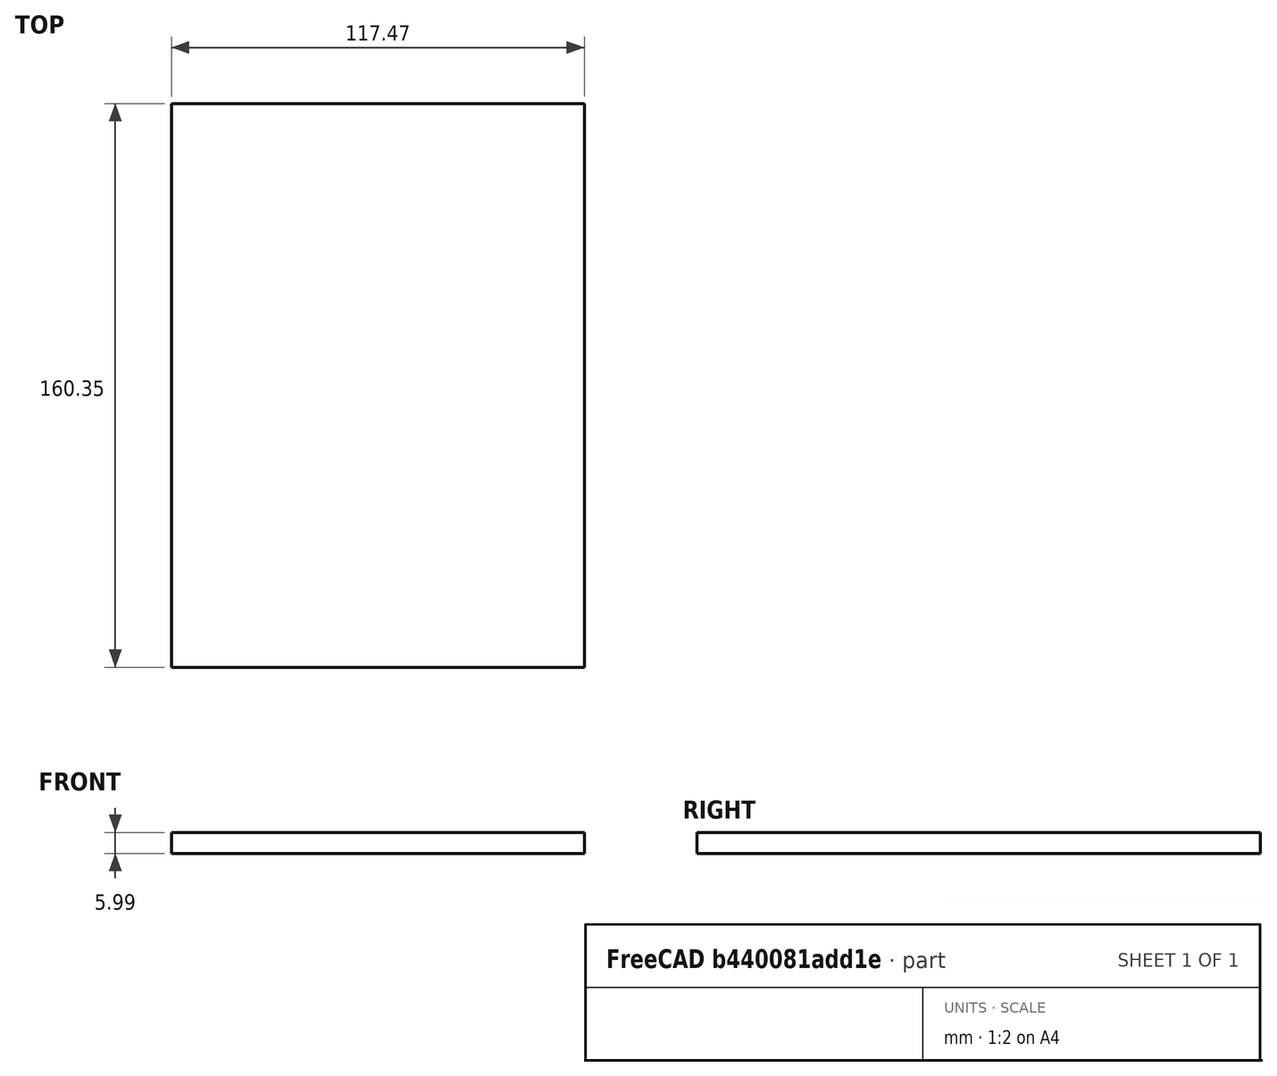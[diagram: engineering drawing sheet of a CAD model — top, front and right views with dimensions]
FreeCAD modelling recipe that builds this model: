
FCSTD DOCUMENT  (FreeCAD 0.19R24267 (Git))
Label: Inv2-P11
License: All rights reserved
LicenseURL: http://en.wikipedia.org/wiki/All_rights_reserved
objects: TechDraw::DrawViewDimension×3, TechDraw::DrawProjGroupItem×2, TechDraw::DrawHatch×2, TechDraw::DrawViewAnnotation×2, Sketcher::SketchObject×1, Part::Extrusion×1, TechDraw::DrawSVGTemplate×1, TechDraw::DrawProjGroup×1, TechDraw::DrawPage×1
note: 2 computed .brp shape members not serialized (recipe doc carries the construction recipe); baked Part::Feature solids carry a one-line shape summary decoded from their .brp

FEATURE [Sketcher::SketchObject] Sketch
  FullyConstrained = true
  sketch-geometry (4):
    g0: LineSegment StartX=0 StartY=0 StartZ=0 EndX=117.475 EndY=0 EndZ=0
    g1: LineSegment StartX=117.475 StartY=0 StartZ=0 EndX=117.475 EndY=-160.35 EndZ=0
    g2: LineSegment StartX=117.475 StartY=-160.35 StartZ=0 EndX=0 EndY=-160.35 EndZ=0
    g3: LineSegment StartX=0 StartY=-160.35 StartZ=0 EndX=0 EndY=0 EndZ=0
  constraints (11):
    c: Coincident(g0,g1)
    c: Coincident(g1,g2)
    c: Coincident(g2,g3)
    c: Coincident(g3,g0)
    c: Horizontal(g0)
    c: Horizontal(g2)
    c: Vertical(g1)
    c: Vertical(g3)
    c: DistanceX(g2,g2) = 117.475
    c: DistanceY(g3,g3) = 160.35
    c: Coincident(g-1,g0)
FEATURE [Part::Extrusion] Extrude
  Base = -> Sketch
  Dir = (0,0,1)
  DirMode = 2
  FaceMakerClass = Part::FaceMakerBullseye
  LengthFwd = 5.9944
  LengthRev = 0
  Solid = true
  Symmetric = false
FEATURE [TechDraw::DrawSVGTemplate] Template
  Height = 215.9
  Orientation = 1
  Width = 279.4
FEATURE [TechDraw::DrawProjGroupItem] ProjItem  label="Front"
  CoarseView = false
  Direction = (0,0,1)
  Focus = 100
  HardHidden = false
  IsoCount = 0
  IsoHidden = false
  IsoVisible = false
  LockPosition = true
  Perspective = false
  Rotation = 0
  RotationVector = (1,0,0)
  Scale = 0.5
  ScaleType = 2
  SeamHidden = false
  SeamVisible = true
  SmoothHidden = false
  SmoothVisible = true
  Source = -> [Extrude]
  Type = 0
  X = 0
  XDirection = (1,0,0)
  Y = 0
FEATURE [TechDraw::DrawProjGroupItem] ProjItem001  label="Left"
  CoarseView = false
  Direction = (-1,0,1e-16)
  Focus = 100
  HardHidden = false
  IsoCount = 0
  IsoHidden = false
  IsoVisible = false
  LockPosition = false
  Perspective = false
  Rotation = 0
  RotationVector = (1,0,0)
  ScaleType = 2
  SeamHidden = false
  SeamVisible = true
  SmoothHidden = false
  SmoothVisible = true
  Source = -> [Extrude]
  Type = 1
  X = 60.3352
  XDirection = (1e-16,0,1)
  Y = 0
FEATURE [TechDraw::DrawProjGroup] ProjGroup
  Anchor = -> ProjItem
  AutoDistribute = true
  LockPosition = false
  ProjectionType = 0
  Rotation = 0
  Scale = 0.5
  ScaleType = 2
  Source = -> [Extrude]
  Views = -> [ProjItem,ProjItem001]
  X = 131.036
  Y = 108.959
  spacingX = 15.0114
  spacingY = 15.0114
FEATURE [TechDraw::DrawHatch] Hatch  label="HatchF0"
  HatchPattern = <path>
  Source = -> ProjItem [Face0]
FEATURE [TechDraw::DrawHatch] Hatch001  label="Hatch001F0"
  HatchPattern = <path>
  Source = -> ProjItem001 [Face0]
FEATURE [TechDraw::DrawViewDimension] Dimension
  Arbitrary = false
  ArbitraryTolerances = false
  EqualTolerance = true
  FormatSpec = %.3f
  FormatSpecOverTolerance = %+.3f
  FormatSpecUnderTolerance = %+.3f
  Inverted = false
  LockPosition = false
  MeasureType = 1
  OverTolerance = 0
  References2D = -> [ProjItem]
  Rotation = 0
  ScaleType = 0
  TheoreticalExact = false
  Type = 1
  UnderTolerance = 0
  X = 0.484314
  Y = -53.164
FEATURE [TechDraw::DrawViewDimension] Dimension001
  Arbitrary = false
  ArbitraryTolerances = false
  EqualTolerance = true
  FormatSpec = %.3f
  FormatSpecOverTolerance = %+.3f
  FormatSpecUnderTolerance = %+.3f
  Inverted = false
  LockPosition = false
  MeasureType = 1
  OverTolerance = 0
  References2D = -> [ProjItem]
  Rotation = 0
  ScaleType = 0
  TheoreticalExact = false
  Type = 2
  UnderTolerance = 0
  X = 36.5327
  Y = -0.511708
FEATURE [TechDraw::DrawViewDimension] Dimension002
  Arbitrary = false
  ArbitraryTolerances = false
  EqualTolerance = true
  FormatSpec = %.3f
  FormatSpecOverTolerance = %+.3f
  FormatSpecUnderTolerance = %+.3f
  Inverted = false
  LockPosition = false
  MeasureType = 1
  OverTolerance = 0
  References2D = -> [ProjItem001]
  Rotation = 0
  ScaleType = 0
  TheoreticalExact = false
  Type = 1
  UnderTolerance = 0
  X = 24.4201
  Y = 28.7366
FEATURE [TechDraw::DrawViewAnnotation] Annotation
  Font = osifont
  LineSpace = 80
  LockPosition = false
  MaxWidth = -1
  Rotation = 0
  ScaleType = 0
  Text = Figure S2 (Inverted 2) | Panel 11 [camera back] | Quantity: 1
  TextSize = 5.0038
  TextStyle = 0
  X = 33.2627
  Y = 195.58
FEATURE [TechDraw::DrawViewAnnotation] Annotation002
  Font = osifont
  LineSpace = 80
  LockPosition = false
  MaxWidth = -1
  Rotation = 0
  ScaleType = 0
  Text = Units: Inches
  TextSize = 5.0038
  TextStyle = 0
  X = 259.08
  Y = 5.08
FEATURE [TechDraw::DrawPage] Page
  KeepUpdated = true
  NextBalloonIndex = 1
  ProjectionType = 0
  Template = -> Template
  Views = -> [ProjGroup,Dimension,Dimension001,Dimension002,Annotation,Annotation002]
note: 2 file-system paths scrubbed to <path> (originals preserved in the JSON sidecar)
